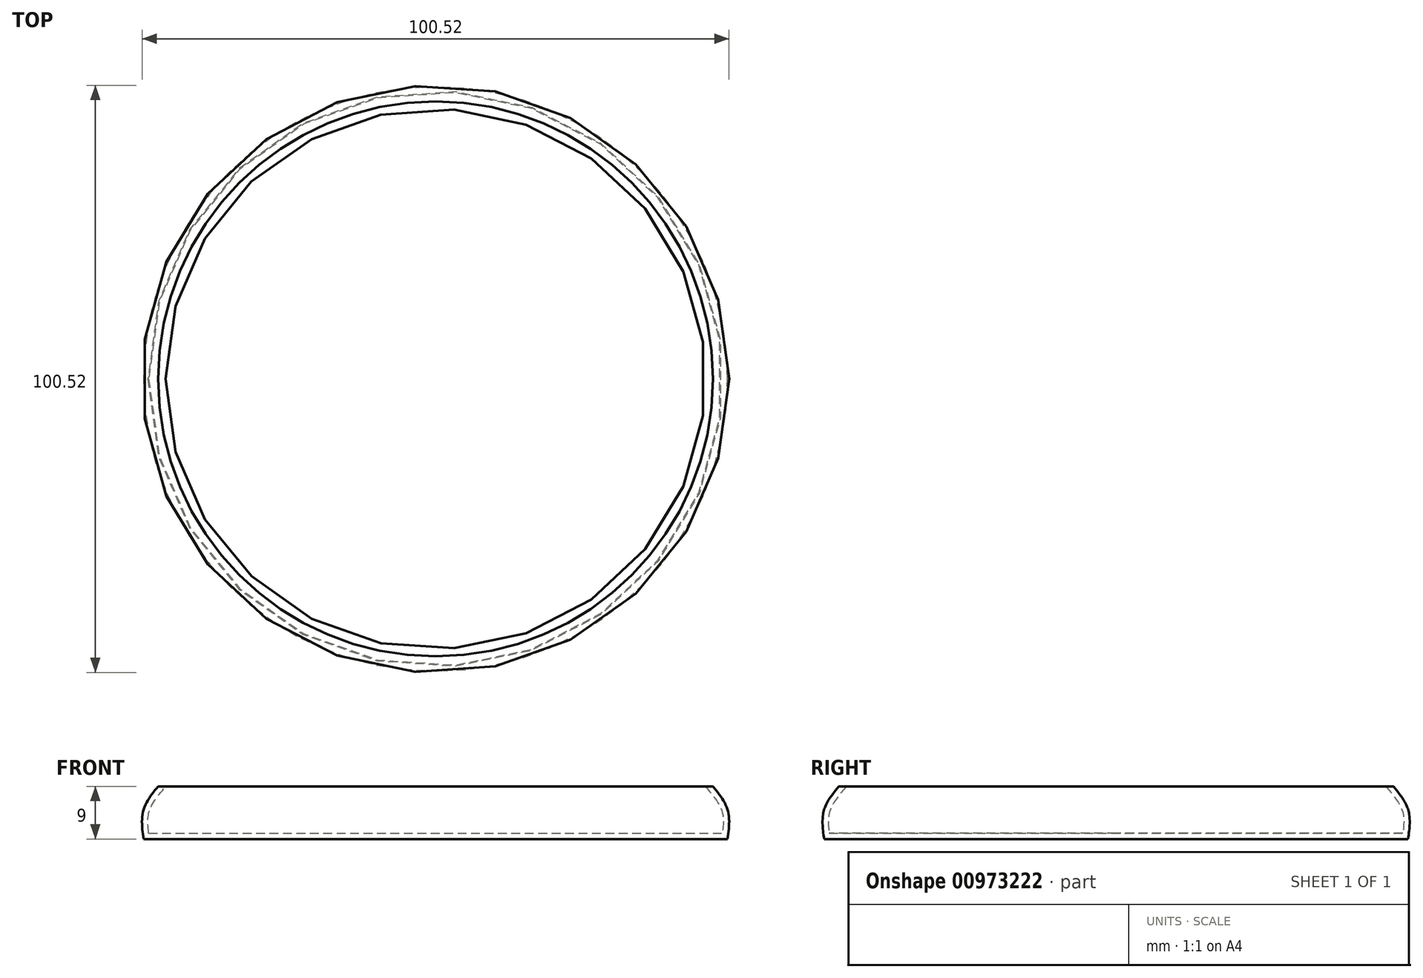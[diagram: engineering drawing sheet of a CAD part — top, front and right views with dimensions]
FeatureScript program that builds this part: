
annotation { "Feature Type Name" : "Feature", "Feature Type Description" : "" }
export const myFeature = defineFeature(function(context is Context, id is Id, definition is map)
    precondition{}
    {
        {
            var Q0;
            Q0=qCreatedBy(makeId("Top.planeOp"),FACE);
            var sketch = newSketch(context, id + "F0", { "sketchPlane" : qUnion([Q0])});
            skCircle(sketch, "E0", {"center": v(0, 0) * mm, "radius": 50 * mm});
            skSolve(sketch);
        }
        {
            var Q0;
            Q0=makeQuery(id+"F0.imprint","IMPRINT",FACE,{"disambiguationData":[TD([[makeQuery(id+"F0.imprint","IMPRINT",EDGE,{"derivedFrom":sQuery(id+"F0.wireOp",EDGE,"E0")}),1.0]])]});
            cPlane(context, id + "F1", {"entities" : qUnion([Q0]), "cplaneType" : CPlaneType.OFFSET, "offset" : 5 * mm, "width" : 150 * mm, "height" : 150 * mm});
        }
        {
            var Q0;
            Q0=qCreatedBy(id+"F1.planeOp",FACE);
            var sketch = newSketch(context, id + "F2", { "sketchPlane" : qUnion([Q0])});
            skCircle(sketch, "E1", {"center": v(0, 0) * mm, "radius": 50 * mm});
            skSolve(sketch);
        }
        {
            var Q0;
            Q0=makeQuery(id+"F2.imprint","IMPRINT",FACE,{"disambiguationData":[TD([[makeQuery(id+"F2.imprint","IMPRINT",EDGE,{"derivedFrom":sQuery(id+"F2.wireOp",EDGE,"E1")}),1.0]])]});
            cPlane(context, id + "F3", {"entities" : qUnion([Q0]), "cplaneType" : CPlaneType.OFFSET, "offset" : 4 * mm, "width" : 150 * mm, "height" : 150 * mm});
        }
        {
            var Q0;
            Q0=qCreatedBy(id+"F3.planeOp",FACE);
            var sketch = newSketch(context, id + "F4", { "sketchPlane" : qUnion([Q0])});
            skCircle(sketch, "E2", {"center": v(0, 0) * mm, "radius": 47.5 * mm});
            skSolve(sketch);
        }
        {
            var Q0;
            Q0=makeQuery(id+"F0.imprint","IMPRINT",FACE,{"disambiguationData":[TD([[makeQuery(id+"F0.imprint","IMPRINT",EDGE,{"derivedFrom":sQuery(id+"F0.wireOp",EDGE,"E0")}),1.0]])]});
            var Q1;
            Q1=makeQuery(id+"F2.imprint","IMPRINT",FACE,{"disambiguationData":[TD([[makeQuery(id+"F2.imprint","IMPRINT",EDGE,{"derivedFrom":sQuery(id+"F2.wireOp",EDGE,"E1")}),1.0]])]});
            var Q2;
            Q2=makeQuery(id+"F4.imprint","IMPRINT",FACE,{"disambiguationData":[TD([[makeQuery(id+"F4.imprint","IMPRINT",EDGE,{"derivedFrom":sQuery(id+"F4.wireOp",EDGE,"E2")}),1.0]])]});
            loft(context, id + "F5", {"sheetProfilesArray" : [{ "sheetProfileEntities" : qUnion([Q0]) }, { "sheetProfileEntities" : qUnion([Q1]) }, { "sheetProfileEntities" : qUnion([Q2]) }]});
        }
        {
            var Q0;
            Q0=makeQuery(id+"F5.opLoft","CAP_FACE",FACE,{"disambiguationData":[OSD([makeQuery(id+"F4.imprint","IMPRINT",FACE,{"disambiguationData":[TD([[makeQuery(id+"F4.imprint","IMPRINT",EDGE,{"derivedFrom":sQuery(id+"F4.wireOp",EDGE,"E2")}),1.0]])]})])],"isStart":true});
            shell(context, id + "F6", {"entities" : qUnion([Q0]), "thickness" : 1 * mm});
        }
    });
